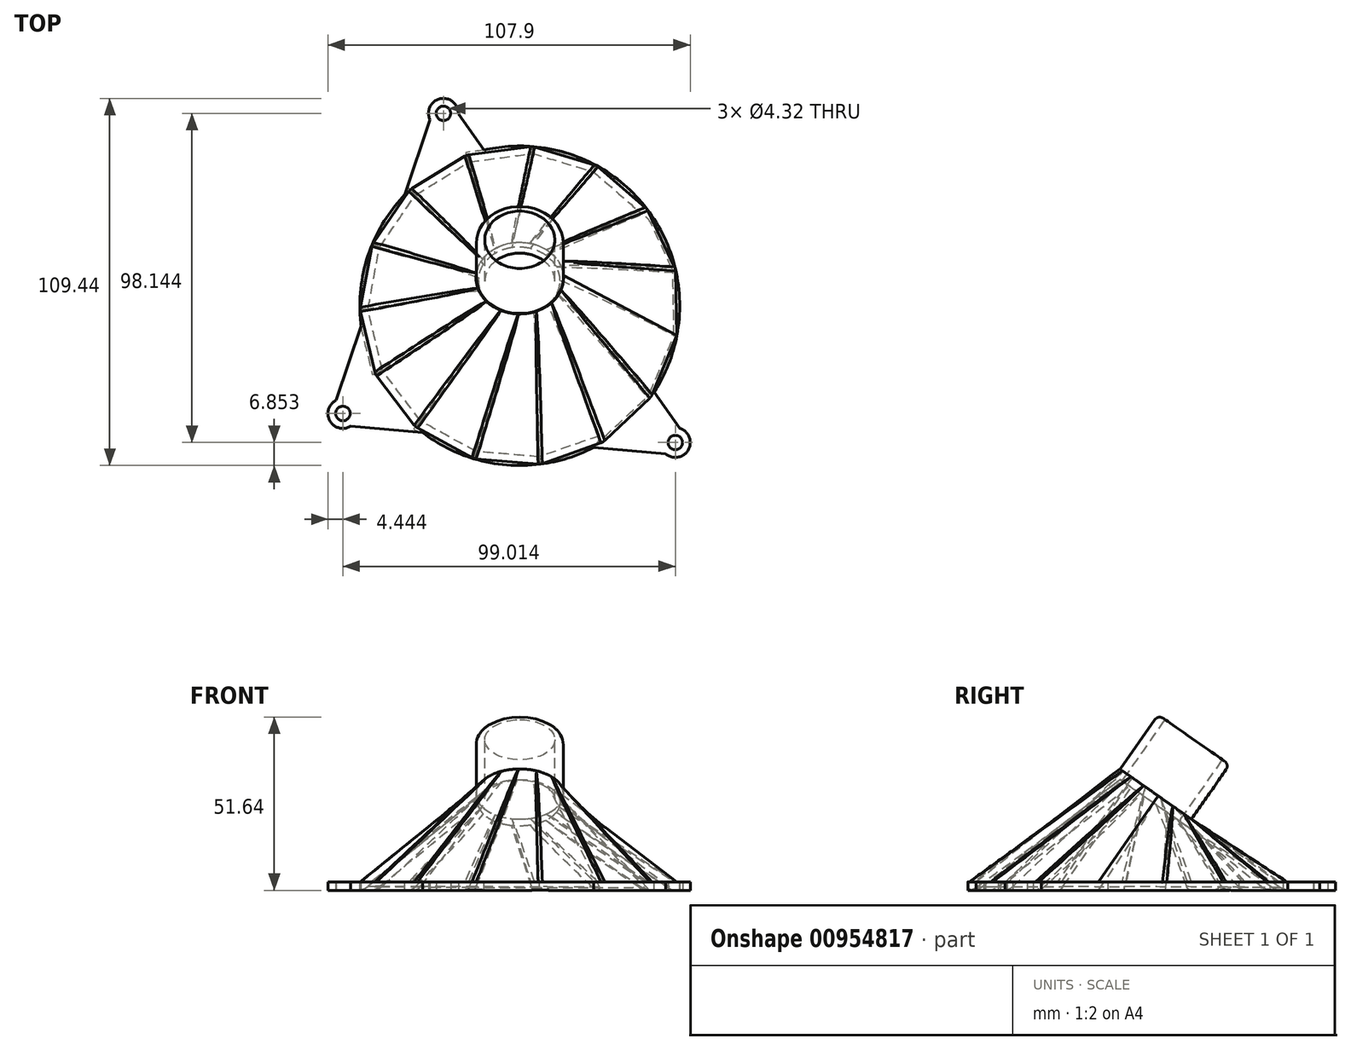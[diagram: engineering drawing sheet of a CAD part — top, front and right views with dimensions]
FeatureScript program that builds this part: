
annotation { "Feature Type Name" : "Feature", "Feature Type Description" : "" }
export const myFeature = defineFeature(function(context is Context, id is Id, definition is map)
    precondition{}
    {
        {
            var Q0;
            Q0=qCreatedBy(makeId("Top.planeOp"),FACE);
            var sketch = newSketch(context, id + "F0", { "sketchPlane" : qUnion([Q0])});
            skPoint(sketch, "E0.middle", {"position": v(0, 0) * mm});
            skLineSegment(sketch, "E1", {"start": v(-23.54, 59.37) * mm, "end": v(-54.54, -33.24) * mm, "construction": true});
            skLineSegment(sketch, "E2", {"start": v(-54.54, -33.24) * mm, "end": v(47.94, -42.2) * mm, "construction": true});
            skLineSegment(sketch, "E3", {"start": v(47.94, -42.2) * mm, "end": v(-23.54, 59.37) * mm, "construction": true});
            skLineSegment(sketch, "E4", {"start": v(-54.54, -33.24) * mm, "end": v(0, 0) * mm, "construction": true});
            skLineSegment(sketch, "E5", {"start": v(-23.54, 59.37) * mm, "end": v(0, 0) * mm, "construction": true});
            skLineSegment(sketch, "E6", {"start": v(0, 0) * mm, "end": v(47.94, -42.2) * mm, "construction": true});
            skCircle(sketch, "E7", {"center": v(-22.74, 57.37) * mm, "radius": 2.16 * mm});
            skCircle(sketch, "E8", {"center": v(46.32, -40.78) * mm, "radius": 2.16 * mm});
            skCircle(sketch, "E9", {"center": v(-52.7, -32.11) * mm, "radius": 2.16 * mm});
            skCircle(sketch, "E10", {"center": v(-52.7, -32.11) * mm, "radius": 4.45 * mm});
            skCircle(sketch, "E11", {"center": v(46.32, -40.78) * mm, "radius": 4.45 * mm});
            skCircle(sketch, "E12", {"center": v(-22.74, 57.37) * mm, "radius": 4.45 * mm});
            skLineSegment(sketch, "E13", {"start": v(-18.3, 57.23) * mm, "end": v(47.69, -36.55) * mm});
            skLineSegment(sketch, "E14", {"start": v(43.4, -44.13) * mm, "end": v(-50.4, -35.92) * mm});
            skLineSegment(sketch, "E15", {"start": v(-54.73, -28.16) * mm, "end": v(-26.74, 55.43) * mm});
            skSolve(sketch);
        }
        {
            var Q0;
            Q0 = qSketchRegion(id + "F0", true);
            extrude(context, id + "F1", {"entities" : qUnion([Q0]), "depth" : 2.54 * mm, "offsetDistance" : 25.4 * mm});
        }
        {
            var Q0;
            Q0 = qSketchRegion(id + "F0", true);
            extrude(context, id + "F2", {"entities" : qUnion([Q0]), "operationType" : NewBodyOperationType.ADD, "depth" : 2.54 * mm, "offsetDistance" : 25.4 * mm});
        }
        {
            var Q0;
            Q0=makeQuery(id+"F1.opExtrude","CAP_FACE",FACE,{"disambiguationData":[OSD([sQuery(id+"F0.wireOp",EDGE,"E7"),sQuery(id+"F0.wireOp",EDGE,"E8"),sQuery(id+"F0.wireOp",EDGE,"E9"),sQuery(id+"F0.wireOp",EDGE,"E10"),sQuery(id+"F0.wireOp",EDGE,"E11"),sQuery(id+"F0.wireOp",EDGE,"E12"),sQuery(id+"F0.wireOp",EDGE,"E13"),sQuery(id+"F0.wireOp",EDGE,"E14"),sQuery(id+"F0.wireOp",EDGE,"E15")])],"isStart":false});
            var sketch = newSketch(context, id + "F3", { "sketchPlane" : qUnion([Q0])});
            skCircle(sketch, "E16", {"center": v(0, 0) * mm, "radius": 47.63 * mm});
            skSolve(sketch);
        }
        {
            var Q0;
            Q0 = qSketchRegion(id + "F3", true);
            extrude(context, id + "F4", {"entities" : qUnion([Q0]), "operationType" : NewBodyOperationType.ADD, "oppositeDirection" : true, "depth" : 2.54 * mm, "offsetDistance" : 25.4 * mm});
        }
        {
            var Q0;
            Q0=qCreatedBy(makeId("Top.planeOp"),FACE);
            cPlane(context, id + "F5", {"entities" : qUnion([Q0]), "cplaneType" : CPlaneType.OFFSET, "offset" : 17.78 * mm, "width" : 152.4 * mm, "height" : 152.4 * mm});
        }
        {
            var Q0;
            Q0=qCreatedBy(id+"F5.planeOp",FACE);
            var sketch = newSketch(context, id + "F6", { "sketchPlane" : qUnion([Q0])});
            skLineSegment(sketch, "E17", {"start": v(-40.31, 23.86) * mm, "end": v(44.77, 23.86) * mm});
            skSolve(sketch);
        }
        {
            var Q0;
            Q0=sQuery(id+"F6.wireOp",EDGE,"E17");
            var Q1;
            Q1=qCreatedBy(id+"F5.planeOp",FACE);
            cPlane(context, id + "F7", {"entities" : qUnion([Q0, Q1]), "cplaneType" : CPlaneType.LINE_ANGLE, "offset" : 25.4 * mm, "angle" : -35 * degree, "width" : 152.4 * mm, "height" : 152.4 * mm});
        }
        {
            var Q0;
            Q0=qCreatedBy(id+"F7.planeOp",FACE);
            var sketch = newSketch(context, id + "F8", { "sketchPlane" : qUnion([Q0])});
            skCircle(sketch, "E18", {"center": v(0, 9.7) * mm, "radius": 13.04 * mm});
            skSolve(sketch);
        }
        {
            var Q0;
            Q0=makeQuery(id+"F4.boolean.opBoolean","MERGE",FACE,{"derivedFrom":[makeQuery(id+"F1.opExtrude","CAP_FACE",FACE,{"disambiguationData":[OSD([sQuery(id+"F0.wireOp",EDGE,"E7"),sQuery(id+"F0.wireOp",EDGE,"E8"),sQuery(id+"F0.wireOp",EDGE,"E9"),sQuery(id+"F0.wireOp",EDGE,"E10"),sQuery(id+"F0.wireOp",EDGE,"E11"),sQuery(id+"F0.wireOp",EDGE,"E12"),sQuery(id+"F0.wireOp",EDGE,"E13"),sQuery(id+"F0.wireOp",EDGE,"E14"),sQuery(id+"F0.wireOp",EDGE,"E15")])],"isStart":false}),makeQuery(id+"F4.opExtrude","CAP_FACE",FACE,{"disambiguationData":[OSD([sQuery(id+"F3.wireOp",EDGE,"E16")])],"isStart":true})]});
            var sketch = newSketch(context, id + "F9", { "sketchPlane" : qUnion([Q0])});
            skCircle(sketch, "E19", {"center": v(0, 0) * mm, "radius": 47.63 * mm});
            skSolve(sketch);
        }
        {
            var Q0;
            Q0=makeQuery(id+"F4.boolean.opBoolean","MERGE",FACE,{"derivedFrom":[makeQuery(id+"F1.opExtrude","CAP_FACE",FACE,{"disambiguationData":[OSD([sQuery(id+"F0.wireOp",EDGE,"E7"),sQuery(id+"F0.wireOp",EDGE,"E8"),sQuery(id+"F0.wireOp",EDGE,"E9"),sQuery(id+"F0.wireOp",EDGE,"E10"),sQuery(id+"F0.wireOp",EDGE,"E11"),sQuery(id+"F0.wireOp",EDGE,"E12"),sQuery(id+"F0.wireOp",EDGE,"E13"),sQuery(id+"F0.wireOp",EDGE,"E14"),sQuery(id+"F0.wireOp",EDGE,"E15")])],"isStart":false}),makeQuery(id+"F4.opExtrude","CAP_FACE",FACE,{"disambiguationData":[OSD([sQuery(id+"F3.wireOp",EDGE,"E16")])],"isStart":true})]});
            var sketch = newSketch(context, id + "F10", { "sketchPlane" : qUnion([Q0])});
            skCircle(sketch, "E20.cCircle", {"center": v(0, 0) * mm, "radius": 46.58 * mm, "construction": true});
            skLineSegment(sketch, "E20.0", {"start": v(39.18, -27.07) * mm, "end": v(24.78, -40.67) * mm});
            skLineSegment(sketch, "E20.1", {"start": v(24.78, -40.67) * mm, "end": v(6.1, -47.23) * mm});
            skLineSegment(sketch, "E20.2", {"start": v(6.1, -47.23) * mm, "end": v(-13.64, -45.63) * mm});
            skLineSegment(sketch, "E20.3", {"start": v(-13.64, -45.63) * mm, "end": v(-31.02, -36.14) * mm});
            skLineSegment(sketch, "E20.4", {"start": v(-31.02, -36.14) * mm, "end": v(-43.04, -20.4) * mm});
            skLineSegment(sketch, "E20.5", {"start": v(-43.04, -20.4) * mm, "end": v(-47.61, -1.13) * mm});
            skLineSegment(sketch, "E20.6", {"start": v(-47.61, -1.13) * mm, "end": v(-43.95, 18.34) * mm});
            skLineSegment(sketch, "E20.7", {"start": v(-43.95, 18.34) * mm, "end": v(-32.7, 34.63) * mm});
            skLineSegment(sketch, "E20.8", {"start": v(-32.7, 34.63) * mm, "end": v(-15.78, 44.93) * mm});
            skLineSegment(sketch, "E20.9", {"start": v(-15.78, 44.93) * mm, "end": v(3.86, 47.47) * mm});
            skLineSegment(sketch, "E20.10", {"start": v(3.86, 47.47) * mm, "end": v(22.83, 41.8) * mm});
            skLineSegment(sketch, "E20.11", {"start": v(22.83, 41.8) * mm, "end": v(37.86, 28.9) * mm});
            skLineSegment(sketch, "E20.12", {"start": v(37.86, 28.9) * mm, "end": v(46.34, 11) * mm});
            skLineSegment(sketch, "E20.13", {"start": v(46.34, 11) * mm, "end": v(46.8, -8.8) * mm});
            skLineSegment(sketch, "E20.14", {"start": v(46.8, -8.8) * mm, "end": v(39.18, -27.07) * mm});
            skPoint(sketch, "E20.0.midPoint", {"position": v(31.98, -33.87) * mm});
            skSolve(sketch);
        }
        {
            var Q0;
            Q0=makeQuery(id+"F10.imprint","IMPRINT",FACE,{"disambiguationData":[TD([[makeQuery(id+"F10.imprint","IMPRINT",EDGE,{"derivedFrom":sQuery(id+"F10.wireOp",EDGE,"E20.0")}),-1.0]])]});
            var Q1;
            Q1=makeQuery(id+"F8.imprint","IMPRINT",FACE,{"disambiguationData":[TD([[makeQuery(id+"F8.imprint","IMPRINT",EDGE,{"derivedFrom":sQuery(id+"F8.wireOp",EDGE,"E18")}),1.0]])]});
            loft(context, id + "F11", {"operationType" : NewBodyOperationType.ADD, "sheetProfilesArray" : [{ "sheetProfileEntities" : qUnion([Q0]) }, { "sheetProfileEntities" : qUnion([Q1]) }]});
        }
        {
            var Q0;
            Q0=makeQuery(id+"F4.boolean.opBoolean","MERGE",FACE,{"derivedFrom":[makeQuery(id+"F1.opExtrude","CAP_FACE",FACE,{"disambiguationData":[OSD([sQuery(id+"F0.wireOp",EDGE,"E7"),sQuery(id+"F0.wireOp",EDGE,"E8"),sQuery(id+"F0.wireOp",EDGE,"E9"),sQuery(id+"F0.wireOp",EDGE,"E10"),sQuery(id+"F0.wireOp",EDGE,"E11"),sQuery(id+"F0.wireOp",EDGE,"E12"),sQuery(id+"F0.wireOp",EDGE,"E13"),sQuery(id+"F0.wireOp",EDGE,"E14"),sQuery(id+"F0.wireOp",EDGE,"E15")])],"isStart":true}),makeQuery(id+"F4.opExtrude","CAP_FACE",FACE,{"disambiguationData":[OSD([sQuery(id+"F3.wireOp",EDGE,"E16")])],"isStart":false})]});
            shell(context, id + "F12", {"entities" : qUnion([Q0]), "thickness" : 2.54 * mm});
        }
        {
            var Q0;
            Q0=makeQuery(id+"F11.opLoft","CAP_FACE",FACE,{"disambiguationData":[OSD([makeQuery(id+"F8.imprint","IMPRINT",FACE,{"disambiguationData":[TD([[makeQuery(id+"F8.imprint","IMPRINT",EDGE,{"derivedFrom":sQuery(id+"F8.wireOp",EDGE,"E18")}),1.0]])]})])],"isStart":true});
            var sketch = newSketch(context, id + "F13", { "sketchPlane" : qUnion([Q0])});
            skCircle(sketch, "E21", {"center": v(0, -9.63) * mm, "radius": 12.96 * mm});
            skSolve(sketch);
        }
        {
            var Q0;
            Q0 = qSketchRegion(id + "F13", true);
            extrude(context, id + "F14", {"entities" : qUnion([Q0]), "operationType" : NewBodyOperationType.ADD, "depth" : 19.8 * mm, "offsetDistance" : 25.4 * mm});
        }
        {
            var Q0;
            Q0=makeQuery(id+"F14.opExtrude","CAP_FACE",FACE,{"disambiguationData":[OSD([sQuery(id+"F13.wireOp",EDGE,"E21")])],"isStart":false});
            var sketch = newSketch(context, id + "F15", { "sketchPlane" : qUnion([Q0])});
            skCircle(sketch, "E22", {"center": v(0, -9.63) * mm, "radius": 10.42 * mm});
            skSolve(sketch);
        }
        {
            var Q0;
            Q0 = qSketchRegion(id + "F15", true);
            extrude(context, id + "F16", {"entities" : qUnion([Q0]), "operationType" : NewBodyOperationType.REMOVE, "oppositeDirection" : true, "depth" : 25.4 * mm, "offsetDistance" : 25.4 * mm});
        }
        {
            var Q0;
            Q0=makeQuery(id+"F11.opLoft","SWEPT_EDGE",EDGE,{"disambiguationData":[OSD([sQuery(id+"F3.wireOp",EDGE,"E16"),sQuery(id+"F8.wireOp",EDGE,"E18"),sQuery(id+"F10.wireOp",EDGE,"E20.11"),sQuery(id+"F10.wireOp",EDGE,"E20.12"),sQuery(id+"F10.wireOp",EDGE,"E20.13")])]});
            var Q1;
            Q1=makeQuery(id+"F11.opLoft","SWEPT_EDGE",EDGE,{"disambiguationData":[OSD([sQuery(id+"F3.wireOp",EDGE,"E16"),sQuery(id+"F8.wireOp",EDGE,"E18"),sQuery(id+"F10.wireOp",EDGE,"E20.12"),sQuery(id+"F10.wireOp",EDGE,"E20.13"),sQuery(id+"F10.wireOp",EDGE,"E20.14")])]});
            var Q2;
            Q2=makeQuery(id+"F11.opLoft","SWEPT_EDGE",EDGE,{"disambiguationData":[OSD([sQuery(id+"F3.wireOp",EDGE,"E16"),sQuery(id+"F8.wireOp",EDGE,"E18"),sQuery(id+"F10.wireOp",EDGE,"E20.0"),sQuery(id+"F10.wireOp",EDGE,"E20.13"),sQuery(id+"F10.wireOp",EDGE,"E20.14")])]});
            var Q3;
            Q3=makeQuery(id+"F11.opLoft","SWEPT_EDGE",EDGE,{"disambiguationData":[OSD([sQuery(id+"F10.wireOp",EDGE,"E20.0"),sQuery(id+"F10.wireOp",EDGE,"E20.14")])]});
            var Q4;
            Q4=makeQuery(id+"F11.opLoft","SWEPT_EDGE",EDGE,{"disambiguationData":[OSD([sQuery(id+"F3.wireOp",EDGE,"E16"),sQuery(id+"F8.wireOp",EDGE,"E18"),sQuery(id+"F10.wireOp",EDGE,"E20.0"),sQuery(id+"F10.wireOp",EDGE,"E20.1"),sQuery(id+"F10.wireOp",EDGE,"E20.2")])]});
            var Q5;
            Q5=makeQuery(id+"F11.opLoft","SWEPT_EDGE",EDGE,{"disambiguationData":[OSD([sQuery(id+"F3.wireOp",EDGE,"E16"),sQuery(id+"F8.wireOp",EDGE,"E18"),sQuery(id+"F10.wireOp",EDGE,"E20.1"),sQuery(id+"F10.wireOp",EDGE,"E20.2"),sQuery(id+"F10.wireOp",EDGE,"E20.3")])]});
            var Q6;
            Q6=makeQuery(id+"F11.opLoft","SWEPT_EDGE",EDGE,{"disambiguationData":[OSD([sQuery(id+"F3.wireOp",EDGE,"E16"),sQuery(id+"F8.wireOp",EDGE,"E18"),sQuery(id+"F10.wireOp",EDGE,"E20.2"),sQuery(id+"F10.wireOp",EDGE,"E20.3"),sQuery(id+"F10.wireOp",EDGE,"E20.4")])]});
            var Q7;
            Q7=makeQuery(id+"F11.opLoft","SWEPT_EDGE",EDGE,{"disambiguationData":[OSD([sQuery(id+"F8.wireOp",EDGE,"E18"),sQuery(id+"F10.wireOp",EDGE,"E20.3"),sQuery(id+"F10.wireOp",EDGE,"E20.4"),sQuery(id+"F10.wireOp",EDGE,"E20.5")])]});
            var Q8;
            Q8=makeQuery(id+"F11.opLoft","SWEPT_EDGE",EDGE,{"disambiguationData":[OSD([sQuery(id+"F3.wireOp",EDGE,"E16"),sQuery(id+"F8.wireOp",EDGE,"E18"),sQuery(id+"F10.wireOp",EDGE,"E20.4"),sQuery(id+"F10.wireOp",EDGE,"E20.5"),sQuery(id+"F10.wireOp",EDGE,"E20.6")])]});
            var Q9;
            Q9=makeQuery(id+"F11.opLoft","SWEPT_EDGE",EDGE,{"disambiguationData":[OSD([sQuery(id+"F3.wireOp",EDGE,"E16"),sQuery(id+"F8.wireOp",EDGE,"E18"),sQuery(id+"F10.wireOp",EDGE,"E20.5"),sQuery(id+"F10.wireOp",EDGE,"E20.6"),sQuery(id+"F10.wireOp",EDGE,"E20.7")])]});
            var Q10;
            Q10=makeQuery(id+"F11.opLoft","SWEPT_EDGE",EDGE,{"disambiguationData":[OSD([sQuery(id+"F3.wireOp",EDGE,"E16"),sQuery(id+"F8.wireOp",EDGE,"E18"),sQuery(id+"F10.wireOp",EDGE,"E20.6"),sQuery(id+"F10.wireOp",EDGE,"E20.7"),sQuery(id+"F10.wireOp",EDGE,"E20.8")])]});
            var Q11;
            Q11=makeQuery(id+"F11.opLoft","SWEPT_EDGE",EDGE,{"disambiguationData":[OSD([sQuery(id+"F8.wireOp",EDGE,"E18"),sQuery(id+"F10.wireOp",EDGE,"E20.7"),sQuery(id+"F10.wireOp",EDGE,"E20.8"),sQuery(id+"F10.wireOp",EDGE,"E20.9")])]});
            var Q12;
            Q12=makeQuery(id+"F11.opLoft","SWEPT_EDGE",EDGE,{"disambiguationData":[OSD([sQuery(id+"F3.wireOp",EDGE,"E16"),sQuery(id+"F8.wireOp",EDGE,"E18"),sQuery(id+"F10.wireOp",EDGE,"E20.8"),sQuery(id+"F10.wireOp",EDGE,"E20.9"),sQuery(id+"F10.wireOp",EDGE,"E20.10")])]});
            var Q13;
            Q13=makeQuery(id+"F11.opLoft","SWEPT_EDGE",EDGE,{"disambiguationData":[OSD([sQuery(id+"F3.wireOp",EDGE,"E16"),sQuery(id+"F8.wireOp",EDGE,"E18"),sQuery(id+"F10.wireOp",EDGE,"E20.9"),sQuery(id+"F10.wireOp",EDGE,"E20.10"),sQuery(id+"F10.wireOp",EDGE,"E20.11")])]});
            var Q14;
            Q14=makeQuery(id+"F11.opLoft","SWEPT_EDGE",EDGE,{"disambiguationData":[OSD([sQuery(id+"F3.wireOp",EDGE,"E16"),sQuery(id+"F8.wireOp",EDGE,"E18"),sQuery(id+"F10.wireOp",EDGE,"E20.10"),sQuery(id+"F10.wireOp",EDGE,"E20.11"),sQuery(id+"F10.wireOp",EDGE,"E20.12")])]});
            var Q15;
            {var subQ0=sQuery(id+"F10.wireOp",EDGE,"E20.4");var subQ1=sQuery(id+"F10.wireOp",EDGE,"E20.3");var subQ2=sQuery(id+"F10.wireOp",EDGE,"E20.2");var subQ3=sQuery(id+"F8.wireOp",EDGE,"E18");var subQ4=sQuery(id+"F3.wireOp",EDGE,"E16");Q15=makeQuery(id+"F12.opShell","OFFSET_EDGE",EDGE,{"disambiguationData":[OSD([subQ4,subQ3,subQ2,subQ1,subQ0]),TDD([makeQuery(id+"F11.opLoft","SWEPT_EDGE",EDGE,{"disambiguationData":[OSD([subQ4,subQ3,subQ2,subQ1,subQ0])]})])]});}
            var Q16;
            {var subQ0=sQuery(id+"F10.wireOp",EDGE,"E20.3");var subQ1=sQuery(id+"F10.wireOp",EDGE,"E20.2");var subQ2=sQuery(id+"F10.wireOp",EDGE,"E20.1");var subQ3=sQuery(id+"F8.wireOp",EDGE,"E18");var subQ4=sQuery(id+"F3.wireOp",EDGE,"E16");Q16=makeQuery(id+"F12.opShell","OFFSET_EDGE",EDGE,{"disambiguationData":[OSD([subQ4,subQ3,subQ2,subQ1,subQ0]),TDD([makeQuery(id+"F11.opLoft","SWEPT_EDGE",EDGE,{"disambiguationData":[OSD([subQ4,subQ3,subQ2,subQ1,subQ0])]})])]});}
            var Q17;
            Q17=makeQuery(id+"F12.opShell","OFFSET_EDGE",EDGE,{"disambiguationData":[OSD([sQuery(id+"F3.wireOp",EDGE,"E16"),sQuery(id+"F8.wireOp",EDGE,"E18"),sQuery(id+"F10.wireOp",EDGE,"E20.0"),sQuery(id+"F10.wireOp",EDGE,"E20.1"),sQuery(id+"F10.wireOp",EDGE,"E20.2")])]});
            var Q18;
            Q18=makeQuery(id+"F12.opShell","OFFSET_EDGE",EDGE,{"disambiguationData":[OSD([sQuery(id+"F10.wireOp",EDGE,"E20.0"),sQuery(id+"F10.wireOp",EDGE,"E20.14")])]});
            var Q19;
            {var subQ0=sQuery(id+"F10.wireOp",EDGE,"E20.14");var subQ1=sQuery(id+"F10.wireOp",EDGE,"E20.13");var subQ2=sQuery(id+"F10.wireOp",EDGE,"E20.0");var subQ3=sQuery(id+"F8.wireOp",EDGE,"E18");var subQ4=sQuery(id+"F3.wireOp",EDGE,"E16");Q19=makeQuery(id+"F12.opShell","OFFSET_EDGE",EDGE,{"disambiguationData":[OSD([subQ4,subQ3,subQ2,subQ1,subQ0]),TDD([makeQuery(id+"F11.opLoft","SWEPT_EDGE",EDGE,{"disambiguationData":[OSD([subQ4,subQ3,subQ2,subQ1,subQ0])]})])]});}
            var Q20;
            {var subQ0=sQuery(id+"F10.wireOp",EDGE,"E20.14");var subQ1=sQuery(id+"F10.wireOp",EDGE,"E20.13");var subQ2=sQuery(id+"F10.wireOp",EDGE,"E20.12");var subQ3=sQuery(id+"F8.wireOp",EDGE,"E18");var subQ4=sQuery(id+"F3.wireOp",EDGE,"E16");Q20=makeQuery(id+"F12.opShell","OFFSET_EDGE",EDGE,{"disambiguationData":[OSD([subQ4,subQ3,subQ2,subQ1,subQ0]),TDD([makeQuery(id+"F11.opLoft","SWEPT_EDGE",EDGE,{"disambiguationData":[OSD([subQ4,subQ3,subQ2,subQ1,subQ0])]})])]});}
            var Q21;
            {var subQ0=sQuery(id+"F10.wireOp",EDGE,"E20.13");var subQ1=sQuery(id+"F10.wireOp",EDGE,"E20.12");var subQ2=sQuery(id+"F10.wireOp",EDGE,"E20.11");var subQ3=sQuery(id+"F8.wireOp",EDGE,"E18");var subQ4=sQuery(id+"F3.wireOp",EDGE,"E16");Q21=makeQuery(id+"F12.opShell","OFFSET_EDGE",EDGE,{"disambiguationData":[OSD([subQ4,subQ3,subQ2,subQ1,subQ0]),TDD([makeQuery(id+"F11.opLoft","SWEPT_EDGE",EDGE,{"disambiguationData":[OSD([subQ4,subQ3,subQ2,subQ1,subQ0])]})])]});}
            var Q22;
            {var subQ0=sQuery(id+"F10.wireOp",EDGE,"E20.12");var subQ1=sQuery(id+"F10.wireOp",EDGE,"E20.11");var subQ2=sQuery(id+"F10.wireOp",EDGE,"E20.10");var subQ3=sQuery(id+"F8.wireOp",EDGE,"E18");var subQ4=sQuery(id+"F3.wireOp",EDGE,"E16");Q22=makeQuery(id+"F12.opShell","OFFSET_EDGE",EDGE,{"disambiguationData":[OSD([subQ4,subQ3,subQ2,subQ1,subQ0]),TDD([makeQuery(id+"F11.opLoft","SWEPT_EDGE",EDGE,{"disambiguationData":[OSD([subQ4,subQ3,subQ2,subQ1,subQ0])]})])]});}
            var Q23;
            {var subQ0=sQuery(id+"F10.wireOp",EDGE,"E20.11");var subQ1=sQuery(id+"F10.wireOp",EDGE,"E20.10");var subQ2=sQuery(id+"F10.wireOp",EDGE,"E20.9");var subQ3=sQuery(id+"F8.wireOp",EDGE,"E18");var subQ4=sQuery(id+"F3.wireOp",EDGE,"E16");Q23=makeQuery(id+"F12.opShell","OFFSET_EDGE",EDGE,{"disambiguationData":[OSD([subQ4,subQ3,subQ2,subQ1,subQ0]),TDD([makeQuery(id+"F11.opLoft","SWEPT_EDGE",EDGE,{"disambiguationData":[OSD([subQ4,subQ3,subQ2,subQ1,subQ0])]})]),OD(1.0)]});}
            var Q24;
            {var subQ0=sQuery(id+"F10.wireOp",EDGE,"E20.10");var subQ1=sQuery(id+"F10.wireOp",EDGE,"E20.9");var subQ2=sQuery(id+"F10.wireOp",EDGE,"E20.8");var subQ3=sQuery(id+"F8.wireOp",EDGE,"E18");var subQ4=sQuery(id+"F3.wireOp",EDGE,"E16");Q24=makeQuery(id+"F12.opShell","OFFSET_EDGE",EDGE,{"disambiguationData":[OSD([subQ4,subQ3,subQ2,subQ1,subQ0]),TDD([makeQuery(id+"F11.opLoft","SWEPT_EDGE",EDGE,{"disambiguationData":[OSD([subQ4,subQ3,subQ2,subQ1,subQ0])]})])]});}
            var Q25;
            {var subQ0=sQuery(id+"F10.wireOp",EDGE,"E20.9");var subQ1=sQuery(id+"F10.wireOp",EDGE,"E20.8");var subQ2=sQuery(id+"F10.wireOp",EDGE,"E20.7");var subQ3=sQuery(id+"F8.wireOp",EDGE,"E18");Q25=makeQuery(id+"F12.opShell","OFFSET_EDGE",EDGE,{"disambiguationData":[OSD([subQ3,subQ2,subQ1,subQ0]),TDD([makeQuery(id+"F11.opLoft","SWEPT_EDGE",EDGE,{"disambiguationData":[OSD([subQ3,subQ2,subQ1,subQ0])]})])]});}
            var Q26;
            {var subQ0=sQuery(id+"F10.wireOp",EDGE,"E20.8");var subQ1=sQuery(id+"F10.wireOp",EDGE,"E20.7");var subQ2=sQuery(id+"F10.wireOp",EDGE,"E20.6");var subQ3=sQuery(id+"F8.wireOp",EDGE,"E18");var subQ4=sQuery(id+"F3.wireOp",EDGE,"E16");Q26=makeQuery(id+"F12.opShell","OFFSET_EDGE",EDGE,{"disambiguationData":[OSD([subQ4,subQ3,subQ2,subQ1,subQ0]),TDD([makeQuery(id+"F11.opLoft","SWEPT_EDGE",EDGE,{"disambiguationData":[OSD([subQ4,subQ3,subQ2,subQ1,subQ0])]})])]});}
            var Q27;
            {var subQ0=sQuery(id+"F10.wireOp",EDGE,"E20.6");var subQ1=sQuery(id+"F10.wireOp",EDGE,"E20.5");var subQ2=sQuery(id+"F10.wireOp",EDGE,"E20.4");var subQ3=sQuery(id+"F8.wireOp",EDGE,"E18");var subQ4=sQuery(id+"F3.wireOp",EDGE,"E16");Q27=makeQuery(id+"F12.opShell","OFFSET_EDGE",EDGE,{"disambiguationData":[OSD([subQ4,subQ3,subQ2,subQ1,subQ0]),TDD([makeQuery(id+"F11.opLoft","SWEPT_EDGE",EDGE,{"disambiguationData":[OSD([subQ4,subQ3,subQ2,subQ1,subQ0])]})])]});}
            var Q28;
            {var subQ0=sQuery(id+"F10.wireOp",EDGE,"E20.5");var subQ1=sQuery(id+"F10.wireOp",EDGE,"E20.4");var subQ2=sQuery(id+"F10.wireOp",EDGE,"E20.3");var subQ3=sQuery(id+"F8.wireOp",EDGE,"E18");Q28=makeQuery(id+"F12.opShell","OFFSET_EDGE",EDGE,{"disambiguationData":[OSD([subQ3,subQ2,subQ1,subQ0]),TDD([makeQuery(id+"F11.opLoft","SWEPT_EDGE",EDGE,{"disambiguationData":[OSD([subQ3,subQ2,subQ1,subQ0])]})])]});}
            var Q29;
            {var subQ0=sQuery(id+"F10.wireOp",EDGE,"E20.7");var subQ1=sQuery(id+"F10.wireOp",EDGE,"E20.6");var subQ2=sQuery(id+"F10.wireOp",EDGE,"E20.5");var subQ3=sQuery(id+"F8.wireOp",EDGE,"E18");var subQ4=sQuery(id+"F3.wireOp",EDGE,"E16");Q29=makeQuery(id+"F12.opShell","OFFSET_EDGE",EDGE,{"disambiguationData":[OSD([subQ4,subQ3,subQ2,subQ1,subQ0]),TDD([makeQuery(id+"F11.opLoft","SWEPT_EDGE",EDGE,{"disambiguationData":[OSD([subQ4,subQ3,subQ2,subQ1,subQ0])]})])]});}
            fillet(context, id + "F17", {"entities" : qUnion([Q0, Q1, Q2, Q3, Q4, Q5, Q6, Q7, Q8, Q9, Q10, Q11, Q12, Q13, Q14, Q15, Q16, Q17, Q18, Q19, Q20, Q21, Q22, Q23, Q24, Q25, Q26, Q27, Q28, Q29]), "tangentPropagation" : true, "radius" : 5.08 * mm, "defaultsChanged" : false, "vertexSettings" : [], "allowEdgeOverflow" : false});
        }
        {
            var Q0;
            Q0=makeQuery(id+"F14.opExtrude","CAP_EDGE",EDGE,{"disambiguationData":[OSD([sQuery(id+"F13.wireOp",EDGE,"E21")])],"isStart":false});
            fillet(context, id + "F18", {"entities" : qUnion([Q0]), "tangentPropagation" : true, "radius" : 1.78 * mm, "defaultsChanged" : true, "vertexSettings" : [], "allowEdgeOverflow" : false});
        }
        {
            var Q0;
            Q0=makeQuery(id+"F16.boolean.opBoolean","COPY",EDGE,{"derivedFrom":makeQuery(id+"F16.opExtrude","CAP_EDGE",EDGE,{"disambiguationData":[OSD([sQuery(id+"F15.wireOp",EDGE,"E22")])],"isStart":true})});
            var Q1;
            Q1=makeQuery(id+"F16.boolean.opBoolean","INTERSECT",EDGE,{"derivedFrom":[makeQuery(id+"F12.opShell","OFFSET_FACE",FACE,{"disambiguationData":[OSD([makeQuery(id+"F8.imprint","IMPRINT",FACE,{"disambiguationData":[TD([[makeQuery(id+"F8.imprint","IMPRINT",EDGE,{"derivedFrom":sQuery(id+"F8.wireOp",EDGE,"E18")}),1.0]])]})])]}),makeQuery(id+"F16.opExtrude","SWEPT_FACE",FACE,{"disambiguationData":[OSD([sQuery(id+"F15.wireOp",EDGE,"E22")])]})]});
            fillet(context, id + "F19", {"entities" : qUnion([Q0, Q1]), "tangentPropagation" : true, "radius" : 0.76 * mm, "defaultsChanged" : false, "vertexSettings" : [], "allowEdgeOverflow" : false});
        }
    });
